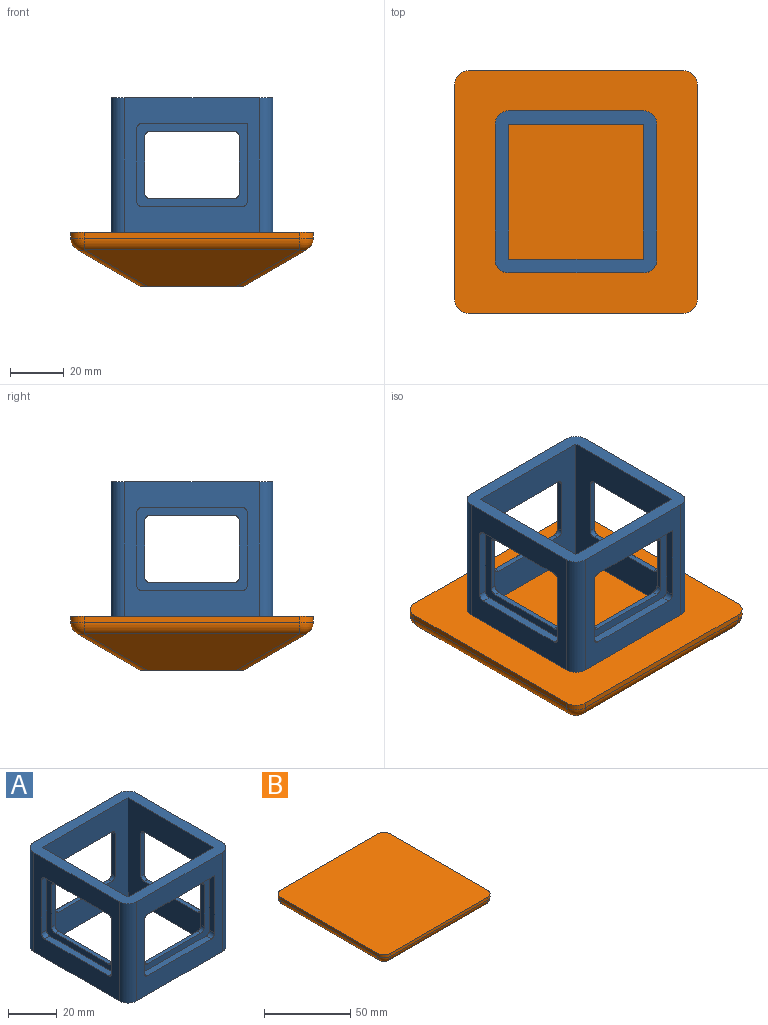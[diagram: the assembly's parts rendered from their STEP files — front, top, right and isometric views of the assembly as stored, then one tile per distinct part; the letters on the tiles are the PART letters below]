
ASSEMBLY  parts=2 mates=1
PART A: 81 faces, bbox 60x60x50 mm
  f0: plane 50x50mm, normal (-1,0,0), area 1232.4mm2, adj f24,f25,f27,f28,f45,f46,f47,f48
  f1: plane 31x2mm, normal (0,0,1), area 62mm2, adj f21,f49,f79,f80
  f2: plane 21x2mm, normal (0,1,0), area 42mm2, adj f21,f49,f78,f79
  f3: plane 31x2mm, normal (0,0,-1), area 62mm2, adj f21,f49,f77,f78
  f4: plane 21x2mm, normal (0,-1,0), area 42mm2, adj f21,f49,f77,f80
  f5: plane 50x50mm, normal (0,1,0), area 1232.4mm2, adj f24,f25,f26,f27,f40,f41,f42,f43
  f6: plane 31x2mm, normal (0,0,-1), area 62mm2, adj f22,f44,f65,f68
  f7: plane 21x2mm, normal (1,0,0), area 42mm2, adj f22,f44,f65,f66
  f8: plane 31x2mm, normal (0,0,1), area 62mm2, adj f22,f44,f66,f67
  f9: plane 21x2mm, normal (-1,0,0), area 42mm2, adj f22,f44,f67,f68
  f10: plane 50x50mm, normal (1,0,0), area 1232.4mm2, adj f24,f25,f26,f29,f35,f36,f37,f38
  f11: plane 21x2mm, normal (0,-1,0), area 42mm2, adj f20,f39,f73,f75
  f12: plane 31x2mm, normal (0,0,-1), area 62mm2, adj f20,f39,f73,f74
  f13: plane 21x2mm, normal (0,1,0), area 42mm2, adj f20,f39,f74,f76
  f14: plane 31x2mm, normal (0,0,1), area 62mm2, adj f20,f39,f75,f76
  f15: plane 50x50mm, normal (0,-1,0), area 1231.6mm2, adj f24,f25,f28,f29,f30,f31,f32,f33
  f16: plane 21x2mm, normal (-1,0,0), area 42mm2, adj f23,f34,f71,f72
  f17: plane 31x2mm, normal (0,0,1), area 62mm2, adj f23,f34,f70,f71
  f18: plane 21x2mm, normal (1,0,0), area 42mm2, adj f23,f34,f69,f70
  f19: plane 31x2mm, normal (0,0,-1), area 62mm2, adj f23,f34,f69,f72
  f20: plane 50x50mm, normal (-1,0,0), area 1628.4mm2, adj f11,f12,f13,f14,f22,f23,f24,f25
  f21: plane 50x50mm, normal (1,0,0), area 1628.4mm2, adj f1,f2,f3,f4,f22,f23,f24,f25
  f22: plane 50x50mm, normal (0,-1,0), area 1628.4mm2, adj f6,f7,f8,f9,f20,f21,f24,f25
  f23: plane 50x50mm, normal (0,1,0), area 1628.4mm2, adj f16,f17,f18,f19,f20,f21,f24,f25
  f24: plane 60x60mm, normal (0,0,1), area 1078.5mm2, adj f0,f5,f10,f15,f20,f21,f22,f23
  f25: plane 60x60mm, normal (0,0,-1), area 1078.5mm2, adj f0,f5,f10,f15,f20,f21,f22,f23
  f26: cylinder r=5mm len=50mm, axis (0,0,1), area 392.7mm2, adj f5,f10,f24,f25
  f27: cylinder r=5mm len=50mm, axis (0,0,-1), area 392.7mm2, adj f0,f5,f24,f25
  f28: cylinder r=5mm len=50mm, axis (0,0,1), area 392.7mm2, adj f0,f15,f24,f25
  f29: cylinder r=5mm len=50mm, axis (0,0,-1), area 392.7mm2, adj f10,f15,f24,f25
  f30: plane 29x3mm, normal (-1,0,0), area 87mm2, adj f15,f31,f34,f64
  f31: plane 39x3mm, normal (0,0,-1), area 117mm2, adj f15,f30,f34,f62
  f32: plane 27x3mm, normal (1,0,0), area 81mm2, adj f15,f34,f62,f63
  f33: plane 37x3mm, normal (0,0,1), area 111mm2, adj f15,f34,f63,f64
  f34: plane 41x31mm, normal (0,-1,0), area 396.9mm2, adj f16,f17,f18,f19,f30,f31,f32,f33
  f35: plane 27x3mm, normal (0,-1,0), area 81mm2, adj f10,f39,f58,f61
  f36: plane 37x3mm, normal (0,0,-1), area 111mm2, adj f10,f39,f58,f59
  f37: plane 27x3mm, normal (0,1,0), area 81mm2, adj f10,f39,f59,f60
  f38: plane 37x3mm, normal (0,0,1), area 111mm2, adj f10,f39,f60,f61
  f39: plane 41x31mm, normal (1,0,0), area 396mm2, adj f11,f12,f13,f14,f35,f36,f37,f38
  f40: plane 27x3mm, normal (1,0,0), area 81mm2, adj f5,f44,f54,f57
  f41: plane 37x3mm, normal (0,0,-1), area 111mm2, adj f5,f44,f54,f55
  f42: plane 27x3mm, normal (-1,0,0), area 81mm2, adj f5,f44,f55,f56
  f43: plane 37x3mm, normal (0,0,1), area 111mm2, adj f5,f44,f56,f57
  f44: plane 41x31mm, normal (0,1,0), area 396mm2, adj f6,f7,f8,f9,f40,f41,f42,f43
  f45: plane 27x3mm, normal (0,1,0), area 81mm2, adj f0,f49,f50,f53
  f46: plane 37x3mm, normal (0,0,-1), area 111mm2, adj f0,f49,f50,f51
  f47: plane 27x3mm, normal (0,-1,0), area 81mm2, adj f0,f49,f51,f52
  f48: plane 37x3mm, normal (0,0,1), area 111mm2, adj f0,f49,f52,f53
  f49: plane 41x31mm, normal (-1,0,0), area 396mm2, adj f1,f2,f3,f4,f45,f46,f47,f48
  f50: cylinder r=2mm len=3mm, axis (-1,0,0), area 9.4mm2, adj f0,f45,f46,f49
  f51: cylinder r=2mm len=3mm, axis (1,0,0), area 9.4mm2, adj f0,f46,f47,f49
  f52: cylinder r=2mm len=3mm, axis (-1,0,0), area 9.4mm2, adj f0,f47,f48,f49
  f53: cylinder r=2mm len=3mm, axis (1,0,0), area 9.4mm2, adj f0,f45,f48,f49
  f54: cylinder r=2mm len=3mm, axis (0,1,0), area 9.4mm2, adj f5,f40,f41,f44
  f55: cylinder r=2mm len=3mm, axis (0,-1,0), area 9.4mm2, adj f5,f41,f42,f44
  f56: cylinder r=2mm len=3mm, axis (0,1,0), area 9.4mm2, adj f5,f42,f43,f44
  f57: cylinder r=2mm len=3mm, axis (0,-1,0), area 9.4mm2, adj f5,f40,f43,f44
  f58: cylinder r=2mm len=3mm, axis (1,0,0), area 9.4mm2, adj f10,f35,f36,f39
  f59: cylinder r=2mm len=3mm, axis (-1,0,0), area 9.4mm2, adj f10,f36,f37,f39
  f60: cylinder r=2mm len=3mm, axis (1,0,0), area 9.4mm2, adj f10,f37,f38,f39
  f61: cylinder r=2mm len=3mm, axis (-1,0,0), area 9.4mm2, adj f10,f35,f38,f39
  f62: cylinder r=2mm len=3mm, axis (0,1,0), area 9.4mm2, adj f15,f31,f32,f34
  f63: cylinder r=2mm len=3mm, axis (0,-1,0), area 9.4mm2, adj f15,f32,f33,f34
  f64: cylinder r=2mm len=3mm, axis (0,1,0), area 9.4mm2, adj f15,f30,f33,f34
  f65: cylinder r=2mm len=2mm, axis (0,1,0), area 6.3mm2, adj f6,f7,f22,f44
  f66: cylinder r=2mm len=2mm, axis (0,-1,0), area 6.3mm2, adj f7,f8,f22,f44
  f67: cylinder r=2mm len=2mm, axis (0,1,0), area 6.3mm2, adj f8,f9,f22,f44
  f68: cylinder r=2mm len=2mm, axis (0,-1,0), area 6.3mm2, adj f6,f9,f22,f44
  f69: cylinder r=2mm len=2mm, axis (0,1,0), area 6.3mm2, adj f18,f19,f23,f34
  f70: cylinder r=2mm len=2mm, axis (0,-1,0), area 6.3mm2, adj f17,f18,f23,f34
  f71: cylinder r=2mm len=2mm, axis (0,1,0), area 6.3mm2, adj f16,f17,f23,f34
  f72: cylinder r=2mm len=2mm, axis (0,-1,0), area 6.3mm2, adj f16,f19,f23,f34
  f73: cylinder r=2mm len=2mm, axis (1,0,0), area 6.3mm2, adj f11,f12,f20,f39
  f74: cylinder r=2mm len=2mm, axis (-1,0,0), area 6.3mm2, adj f12,f13,f20,f39
  f75: cylinder r=2mm len=2mm, axis (-1,0,0), area 6.3mm2, adj f11,f14,f20,f39
  f76: cylinder r=2mm len=2mm, axis (1,0,0), area 6.3mm2, adj f13,f14,f20,f39
  f77: cylinder r=2mm len=2mm, axis (1,0,0), area 6.3mm2, adj f3,f4,f21,f49
  f78: cylinder r=2mm len=2mm, axis (-1,0,0), area 6.3mm2, adj f2,f3,f21,f49
  f79: cylinder r=2mm len=2mm, axis (1,0,0), area 6.3mm2, adj f1,f2,f21,f49
  f80: cylinder r=2mm len=2mm, axis (-1,0,0), area 6.3mm2, adj f1,f4,f21,f49
PART B: 26 faces, bbox 90x90x20.3 mm
  f0: plane 80x2.11mm, normal (1,0,0), area 169.1mm2, adj f4,f10,f12,f22
  f1: plane 80x2.11mm, normal (0,1,0), area 169.1mm2, adj f4,f10,f14,f18
  f2: plane 80x2.11mm, normal (-1,0,0), area 169.1mm2, adj f4,f14,f16,f21
  f3: plane 80x2.11mm, normal (0,-1,0), area 169.1mm2, adj f4,f12,f16,f25
  f4: plane 90x90mm, normal (0,0,1), area 8078.5mm2, adj f0,f1,f2,f3,f10,f12,f14,f16
  f5: plane 38.04x38.04mm, normal (0,0,-1), area 1442.5mm2, adj f6,f7,f8,f9,f11,f13,f15,f17
  f6: plane 80x23.48mm, normal (0.5,0,-0.87), area 1532.4mm2, adj f5,f11,f13,f22
  f7: plane 80x23.48mm, normal (0,0.5,-0.87), area 1532.4mm2, adj f5,f11,f15,f18
  f8: plane 80x23.48mm, normal (0,-0.5,-0.87), area 1532.4mm2, adj f5,f13,f17,f25
  f9: plane 80x23.48mm, normal (-0.5,0,-0.87), area 1532.4mm2, adj f5,f15,f17,f21
  f10: cylinder r=5mm len=5mm, axis (0,0,1), area 16.6mm2, adj f0,f1,f4,f20
  f11: cylinder r=5mm len=25.98mm, axis (0.65,0.65,0.38), area 127.7mm2, adj f5,f6,f7,f20
  f12: cylinder r=5mm len=5mm, axis (0,0,-1), area 16.6mm2, adj f0,f3,f4,f24
  f13: cylinder r=5mm len=25.98mm, axis (0.65,-0.65,0.38), area 127.7mm2, adj f5,f6,f8,f24
  f14: cylinder r=5mm len=5mm, axis (0,0,-1), area 16.6mm2, adj f1,f2,f4,f19
  f15: cylinder r=5mm len=25.98mm, axis (0.65,-0.65,-0.38), area 127.7mm2, adj f5,f7,f9,f19
  f16: cylinder r=5mm len=5mm, axis (0,0,1), area 16.6mm2, adj f2,f3,f4,f23
  f17: cylinder r=5mm len=25.98mm, axis (0.65,0.65,-0.38), area 127.7mm2, adj f5,f8,f9,f23
  f18: cylinder r=5mm len=80mm, axis (-1,0,0), area 418.9mm2, adj f1,f7,f19,f20
  f19: sphere r=5mm, area 35.7mm2, adj f14,f15,f18,f21
  f20: sphere r=5mm, area 35.7mm2, adj f10,f11,f18,f22
  f21: cylinder r=5mm len=80mm, axis (0,-1,0), area 418.9mm2, adj f2,f9,f19,f23
  f22: cylinder r=5mm len=80mm, axis (0,1,0), area 418.9mm2, adj f0,f6,f20,f24
  f23: sphere r=5mm, area 35.7mm2, adj f16,f17,f21,f25
  f24: sphere r=5mm, area 35.7mm2, adj f12,f13,f22,f25
  f25: cylinder r=5mm len=80mm, axis (1,0,0), area 418.9mm2, adj f3,f8,f23,f24
PLACE A t=(-7.53,-4.99,6.56)mm
PLACE B t=(-7.53,-4.99,-13.44)mm fixed
MATE fastened B.f4 <-> A.f25  axis (0,0,1) through (-7.53,-4.99,6.56)mm
